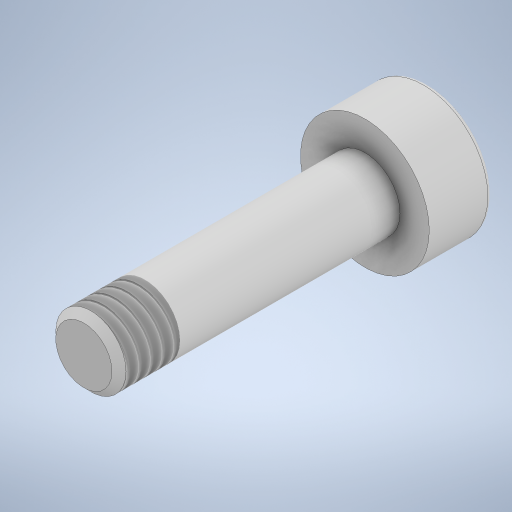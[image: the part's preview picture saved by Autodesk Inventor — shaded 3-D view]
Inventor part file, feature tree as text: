
AUTODESK INVENTOR PART (.ipt)
format: ipt  version: 2024 (Build 280153000, 153)  size: 301,056 bytes
history: native  units: in
note: dims shown in document units (in); Inventor stores cm internally (conversion verified against a paired STEP export)
features: extrude x3, sketch x2, plane x1, chamfer x1, fillet x1, thread x1, direct_edit x1, other x1
ambient origin geometry x8: Origin, YZ Plane, XZ Plane, XY Plane, X Axis, Y Axis, Z Axis, Center Point
bodies: Solid1 (feature_tree)
feature tree (11):
  sketch  "Sketch1"  dims[d0=0.2165in d1=0.1137in]
  extrude  "Extrusion1"  Depth=0.1137in
  extrude  "Extrusion2"  Depth=0.3937in TaperAngle=0.0deg
  plane  "Work Plane1"
  extrude  "Extrusion3"  TaperAngle=0.0deg  [1 undecoded]
  chamfer  "Chamfer1"  Distance=0.1181in
  fillet  "Fillet1"  Radius=0.4724in
  thread  "Thread1"  [1 undecoded]
  direct_edit  "Direct Edit1"
  sketch  "Sketch2"  dims[d2=0.1063in d3=0.0in d4=0.0492in d5=0.0in d6=0.0in d7=0.1181in d8=0.4724in d9=0.0in d10=0.0118in d11=0.0787in d12=45.0deg d13=0.0079in d14=0.3937in d15=0.0in d16=3.937in d17=0.3937in d18=0.3937in]
  other  "Scale1"
note: 2 required parameter values undecoded (feature->parameter linkage not recoverable at this tier; creation-order binding heuristic only, values carry confidence <= 0.55)
